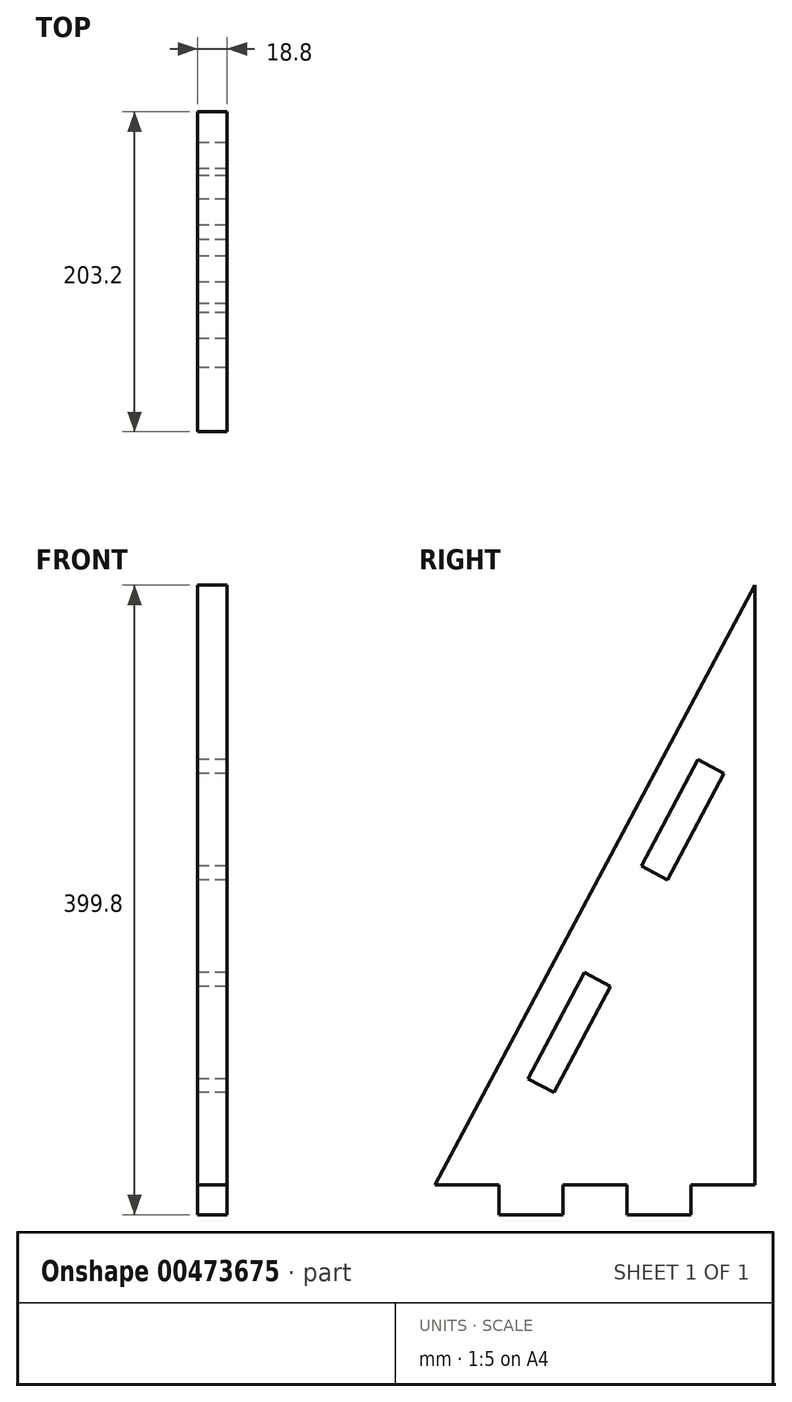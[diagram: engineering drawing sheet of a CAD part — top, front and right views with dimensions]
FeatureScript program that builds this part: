
annotation { "Feature Type Name" : "Feature", "Feature Type Description" : "" }
export const myFeature = defineFeature(function(context is Context, id is Id, definition is map)
    precondition{}
    {
        {
            var Q0;
            Q0=qCreatedBy(makeId("Right.planeOp"),FACE);
            var sketch = newSketch(context, id + "F0", { "sketchPlane" : qUnion([Q0])});
            skLineSegment(sketch, "E0", {"start": v(0, 0) * mm, "end": v(0, 381) * mm});
            skLineSegment(sketch, "E1", {"start": v(0, 381) * mm, "end": v(-203.2, 0) * mm});
            skLineSegment(sketch, "E2", {"start": v(-203.2, 0) * mm, "end": v(0, 0) * mm});
            skLineSegment(sketch, "E3.0", {"start": v(17.93, 371.44) * mm, "end": v(-185.27, -9.56) * mm});
            skPoint(sketch, "E4", {"position": v(0, 337.82) * mm});
            skPoint(sketch, "E5", {"position": v(-180.17, 0) * mm});
            skLineSegment(sketch, "E6", {"start": v(-180.17, 0) * mm, "end": v(-144.14, 67.56) * mm});
            skLineSegment(sketch, "E7", {"start": v(-144.14, 67.56) * mm, "end": v(-127.55, 58.72) * mm});
            skLineSegment(sketch, "E8", {"start": v(-127.55, 58.72) * mm, "end": v(-91.52, 126.28) * mm});
            skLineSegment(sketch, "E9", {"start": v(-91.52, 126.28) * mm, "end": v(-108.1, 135.13) * mm});
            skLineSegment(sketch, "E10", {"start": v(-108.1, 135.13) * mm, "end": v(-72.07, 202.69) * mm});
            skLineSegment(sketch, "E11", {"start": v(-72.07, 202.69) * mm, "end": v(-55.49, 193.84) * mm});
            skLineSegment(sketch, "E12", {"start": v(-55.49, 193.84) * mm, "end": v(-19.45, 261.4) * mm});
            skLineSegment(sketch, "E13", {"start": v(-19.45, 261.4) * mm, "end": v(-36.04, 270.25) * mm});
            skLineSegment(sketch, "E14", {"start": v(-36.04, 270.25) * mm, "end": v(0, 337.82) * mm});
            skLineSegment(sketch, "E15", {"start": v(-101.6, 0) * mm, "end": v(-162.56, 0) * mm});
            skLineSegment(sketch, "E16", {"start": v(-162.56, 0) * mm, "end": v(-162.56, -18.8) * mm});
            skLineSegment(sketch, "E17", {"start": v(-162.56, -18.8) * mm, "end": v(-121.92, -18.8) * mm});
            skLineSegment(sketch, "E18", {"start": v(-121.92, -18.8) * mm, "end": v(-121.92, 0) * mm});
            skLineSegment(sketch, "E19", {"start": v(-121.92, 0) * mm, "end": v(-162.56, 0) * mm});
            skLineSegment(sketch, "E20", {"start": v(-101.6, 0) * mm, "end": v(-40.64, 0) * mm});
            skLineSegment(sketch, "E21", {"start": v(-40.64, 0) * mm, "end": v(-40.64, -18.8) * mm});
            skLineSegment(sketch, "E22", {"start": v(-40.64, -18.8) * mm, "end": v(-81.28, -18.8) * mm});
            skLineSegment(sketch, "E23", {"start": v(-81.28, -18.8) * mm, "end": v(-81.28, 0) * mm});
            skLineSegment(sketch, "E24", {"start": v(-81.28, 0) * mm, "end": v(-40.64, 0) * mm});
            skSolve(sketch);
        }
        {
            var Q0;
            Q0 = qSketchRegion(id + "F0", true);
            extrude(context, id + "F1", {"entities" : qUnion([Q0]), "depth" : 18.8 * mm});
        }
    });
